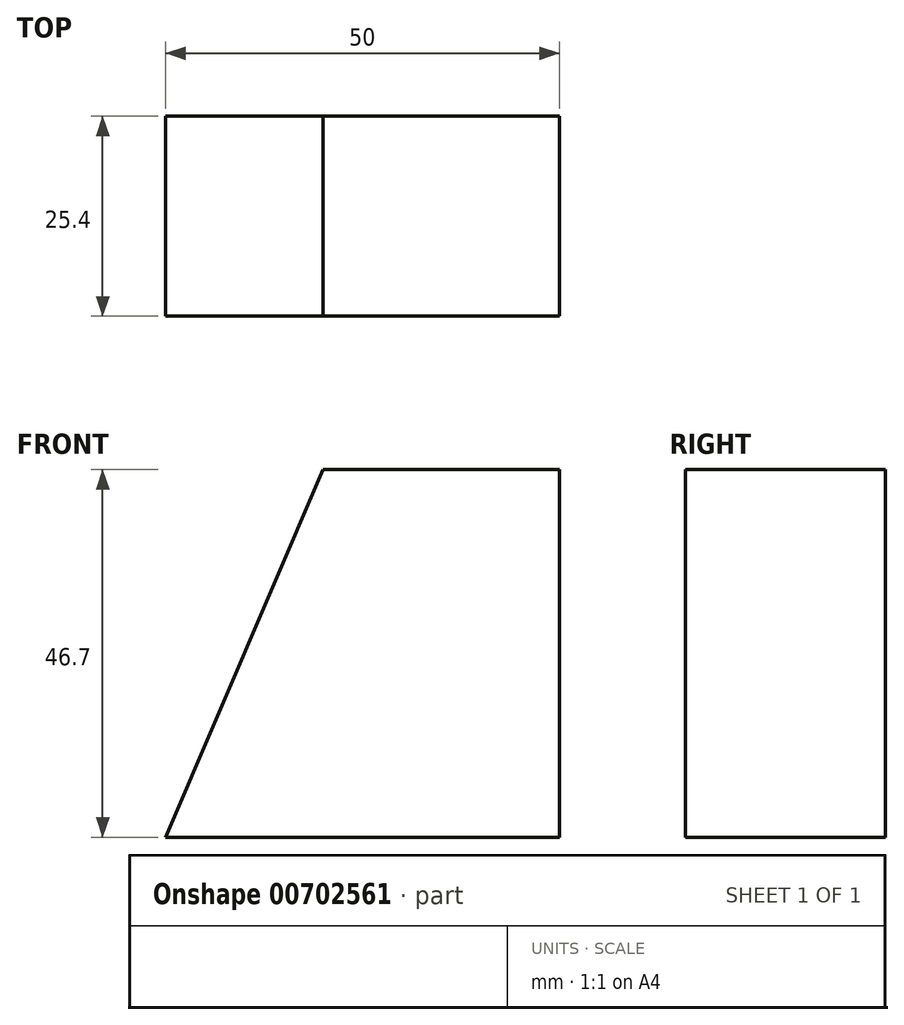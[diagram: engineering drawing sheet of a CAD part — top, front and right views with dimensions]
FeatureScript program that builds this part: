
annotation { "Feature Type Name" : "Feature", "Feature Type Description" : "" }
export const myFeature = defineFeature(function(context is Context, id is Id, definition is map)
    precondition{}
    {
        {
            var Q0;
            Q0=qCreatedBy(makeId("Front.planeOp"),FACE);
            var sketch = newSketch(context, id + "F0", { "sketchPlane" : qUnion([Q0])});
            skLineSegment(sketch, "E0", {"start": v(0, 0) * mm, "end": v(50, 0) * mm});
            skLineSegment(sketch, "E1", {"start": v(50, 0) * mm, "end": v(50, 46.7) * mm});
            skLineSegment(sketch, "E2", {"start": v(50, 46.7) * mm, "end": v(20, 46.7) * mm});
            skLineSegment(sketch, "E3", {"start": v(20, 46.7) * mm, "end": v(0, 0) * mm});
            skSolve(sketch);
        }
        {
            var Q0;
            Q0 = qSketchRegion(id + "F0", true);
            extrude(context, id + "F1", {"entities" : qUnion([Q0]), "depth" : 25.4 * mm, "offsetDistance" : 25.4 * mm});
        }
    });
